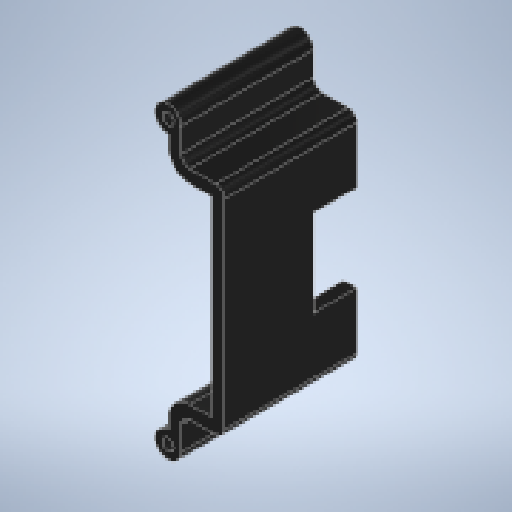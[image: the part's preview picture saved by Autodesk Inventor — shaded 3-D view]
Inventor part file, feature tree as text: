
AUTODESK INVENTOR PART (.ipt)
format: ipt  version: 2025.1 (Build 291241000, 241)  size: 177,664 bytes
history: native  units: mm
features: other x5, sketch x1, extrude x1, reference x1
ambient origin geometry x8: Origin, YZ Plane, XZ Plane, XY Plane, X Axis, Y Axis, Z Axis, Center Point
bodies: Body1 (feature_tree)
feature tree (8):
  other  "ソリッド1"
  sketch  "スケッチ1"
  other  "作業平面1"
  extrude  "押し出し1"  Depth=6.0mm
  reference  "参照1"
  other  "<userpath>\Documents\Inventor\Vixen\doutai.iam"
  other  "doutai.iam"
  other  "kataue:1"
